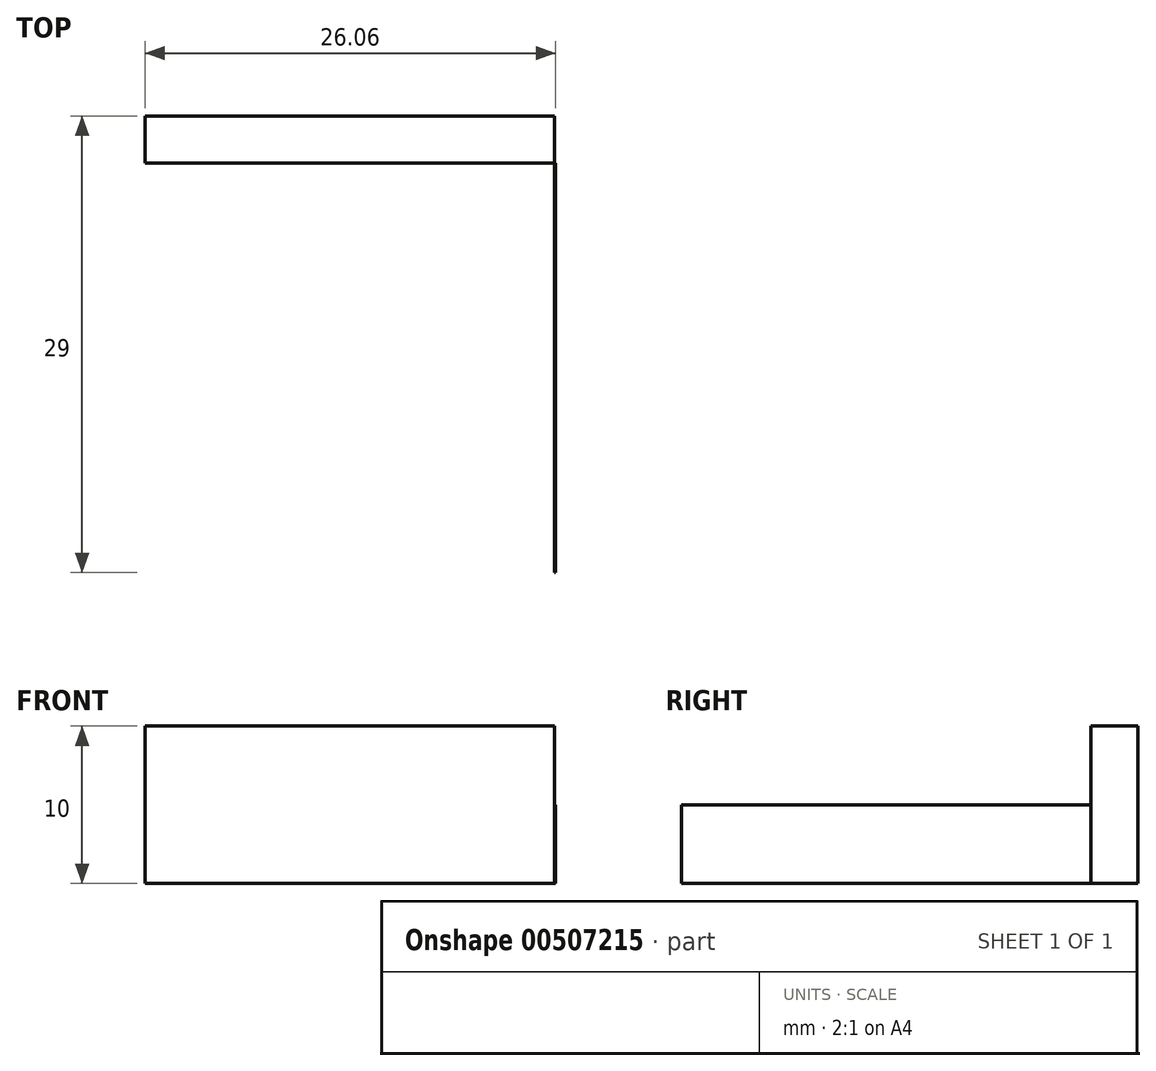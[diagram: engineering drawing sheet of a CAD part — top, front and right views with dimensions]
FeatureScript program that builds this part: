
annotation { "Feature Type Name" : "Feature", "Feature Type Description" : "" }
export const myFeature = defineFeature(function(context is Context, id is Id, definition is map)
    precondition{}
    {
        {
            var Q0;
            Q0=qCreatedBy(makeId("Top.planeOp"),FACE);
            var sketch = newSketch(context, id + "F0", { "sketchPlane" : qUnion([Q0])});
            skLineSegment(sketch, "E0.bottom", {"start": v(13.03, 13) * mm, "end": v(-13.03, 13) * mm});
            skLineSegment(sketch, "E0.top", {"start": v(13.03, -13) * mm, "end": v(-13.03, -13) * mm});
            skLineSegment(sketch, "E0.left", {"start": v(13.03, 13) * mm, "end": v(13.03, -13) * mm});
            skLineSegment(sketch, "E0.right", {"start": v(-13.03, 13) * mm, "end": v(-13.03, -13) * mm});
            skPoint(sketch, "E0.middle", {"position": v(0, 0) * mm});
            skLineSegment(sketch, "E1.bottom", {"start": v(-13.03, 13) * mm, "end": v(12.97, 13) * mm});
            skLineSegment(sketch, "E1.top", {"start": v(-13.03, 16) * mm, "end": v(12.97, 16) * mm});
            skLineSegment(sketch, "E1.left", {"start": v(-13.03, 13) * mm, "end": v(-13.03, 16) * mm});
            skLineSegment(sketch, "E1.right", {"start": v(12.97, 13) * mm, "end": v(12.97, 16) * mm});
            skLineSegment(sketch, "E2.bottom", {"start": v(12.97, 16) * mm, "end": v(16.19, 16) * mm});
            skLineSegment(sketch, "E2.top", {"start": v(12.97, -13) * mm, "end": v(16.19, -13) * mm});
            skLineSegment(sketch, "E2.left", {"start": v(12.97, 16) * mm, "end": v(12.97, -13) * mm});
            skLineSegment(sketch, "E2.right", {"start": v(16.19, 16) * mm, "end": v(16.19, -13) * mm});
            skCircle(sketch, "E3", {"center": v(4.92, 3.95) * mm, "radius": 2.05 * mm});
            skSolve(sketch);
        }
        {
            var Q0;
            {var subQ4=sQuery(id+"F0.wireOp",EDGE,"E0.bottom");Q0=makeQuery(id+"F0.imprint","IMPRINT",FACE,{"disambiguationData":[TD([[makeQuery(id+"F0.imprint","IMPRINT",EDGE,{"derivedFrom":subQ4}),-1.0]])]});}
            var Q1;
            {var subQ0=sQuery(id+"F0.wireOp",EDGE,"E1.bottom");Q1=makeQuery(id+"F0.imprint","IMPRINT",FACE,{"disambiguationData":[TD([[makeQuery(id+"F0.imprint","IMPRINT",EDGE,{"derivedFrom":subQ0}),1.0]])]});}
            extrude(context, id + "F1", {"entities" : qUnion([Q0, Q1]), "depth" : 10 * mm, "offsetDistance" : 25 * mm});
        }
        {
            var Q0;
            {var subQ2=sQuery(id+"F0.wireOp",EDGE,"E0.top");Q0=makeQuery(id+"F0.imprint","IMPRINT",FACE,{"disambiguationData":[TD([[makeQuery(id+"F0.imprint","IMPRINT",EDGE,{"derivedFrom":subQ2}),-1.0]])]});}
            extrude(context, id + "F2", {"entities" : qUnion([Q0]), "operationType" : NewBodyOperationType.ADD, "depth" : 5 * mm, "offsetDistance" : 25 * mm});
        }
    });
